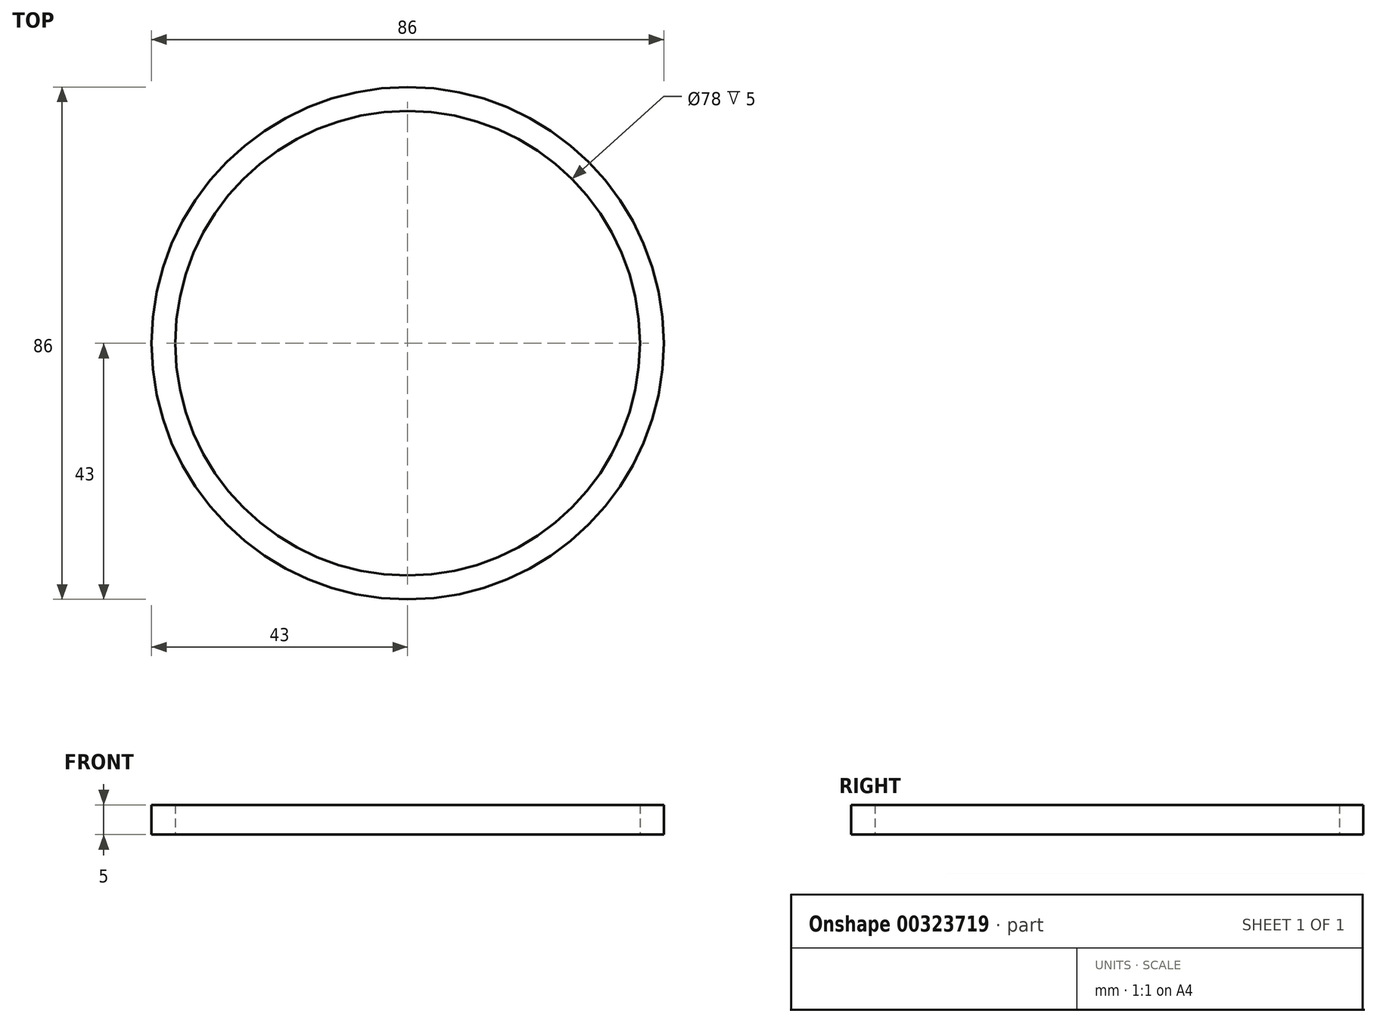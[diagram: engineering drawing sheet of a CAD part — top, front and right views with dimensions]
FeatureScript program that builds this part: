
annotation { "Feature Type Name" : "Feature", "Feature Type Description" : "" }
export const myFeature = defineFeature(function(context is Context, id is Id, definition is map)
    precondition{}
    {
        {
            var Q0;
            Q0=qCreatedBy(makeId("Top.planeOp"),FACE);
            var sketch = newSketch(context, id + "F0", { "sketchPlane" : qUnion([Q0])});
            skCircle(sketch, "E0", {"center": v(0, 0) * mm, "radius": 39 * mm});
            skCircle(sketch, "E1.0", {"center": v(0, 0) * mm, "radius": 43 * mm});
            skSolve(sketch);
        }
        {
            var Q0;
            Q0 = qSketchRegion(id + "F0", true);
            extrude(context, id + "F1", {"entities" : qUnion([Q0]), "depth" : 5 * mm});
        }
    });
